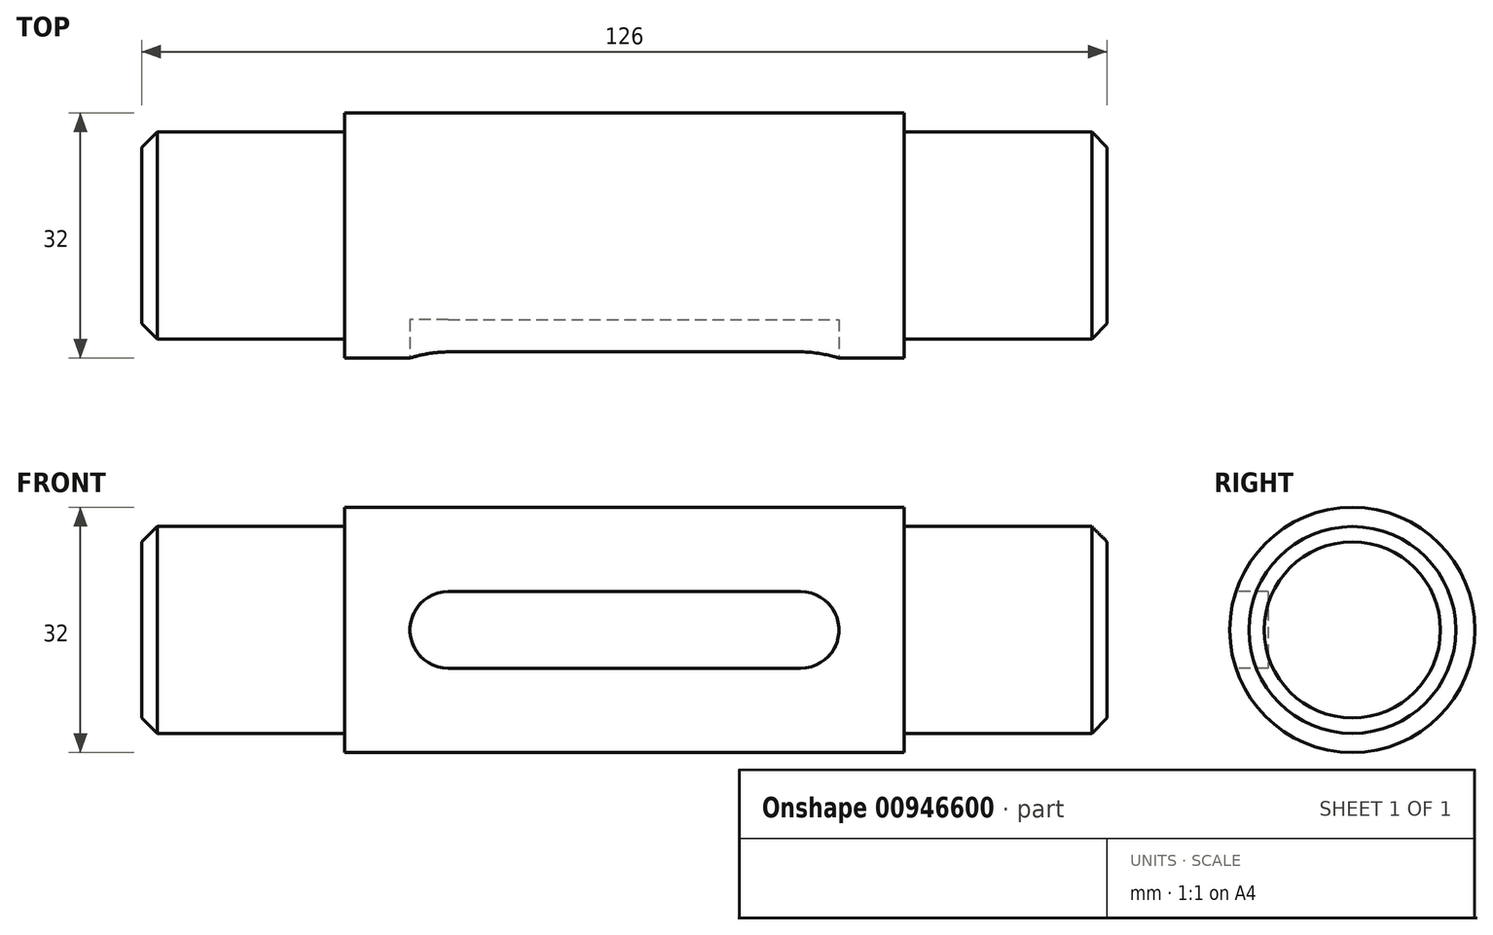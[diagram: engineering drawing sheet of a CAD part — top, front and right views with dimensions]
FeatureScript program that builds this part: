
annotation { "Feature Type Name" : "Feature", "Feature Type Description" : "" }
export const myFeature = defineFeature(function(context is Context, id is Id, definition is map)
    precondition{}
    {
        {
            var Q0;
            Q0=qCreatedBy(makeId("Front.planeOp"),FACE);
            var sketch = newSketch(context, id + "F0", { "sketchPlane" : qUnion([Q0])});
            skLineSegment(sketch, "E0", {"start": v(0, 16) * mm, "end": v(-36.5, 16) * mm});
            skLineSegment(sketch, "E1", {"start": v(-36.5, 16) * mm, "end": v(-36.5, 13.5) * mm});
            skLineSegment(sketch, "E2", {"start": v(-36.5, 13.5) * mm, "end": v(-61, 13.5) * mm});
            skLineSegment(sketch, "E3", {"start": v(-61, 13.5) * mm, "end": v(-63, 11.5) * mm});
            skLineSegment(sketch, "E4", {"start": v(-63, 11.5) * mm, "end": v(-63, 0) * mm});
            skLineSegment(sketch, "E5.MirrorCS", {"start": v(0, 16) * mm, "end": v(36.5, 16) * mm});
            skLineSegment(sketch, "E6.MirrorCS", {"start": v(36.5, 16) * mm, "end": v(36.5, 13.5) * mm});
            skLineSegment(sketch, "E7.MirrorCS", {"start": v(36.5, 13.5) * mm, "end": v(61, 13.5) * mm});
            skLineSegment(sketch, "E8.MirrorCS", {"start": v(61, 13.5) * mm, "end": v(63, 11.5) * mm});
            skLineSegment(sketch, "E9.MirrorCS", {"start": v(63, 11.5) * mm, "end": v(63, 0) * mm});
            skLineSegment(sketch, "E10", {"start": v(-63, 0) * mm, "end": v(63, 0) * mm});
            skSolve(sketch);
        }
        {
            var Q0;
            Q0 = qSketchRegion(id + "F0", true);
            var Q1;
            Q1=sQuery(id+"F0.wireOp",EDGE,"E10");
            revolve(context, id + "F1", {"surfaceOperationType" : NewSurfaceOperationType.NEW, "entities" : qUnion([Q0]), "axis" : qUnion([Q1]), "revolveType" : RevolveType.FULL});
        }
        {
            var Q0;
            Q0=qCreatedBy(makeId("Front.planeOp"),FACE);
            cPlane(context, id + "F2", {"entities" : qUnion([Q0]), "cplaneType" : CPlaneType.OFFSET, "offset" : 16 * mm, "width" : 150 * mm, "height" : 150 * mm});
        }
        {
            var Q0;
            Q0=qCreatedBy(id+"F2.planeOp",FACE);
            var sketch = newSketch(context, id + "F3", { "sketchPlane" : qUnion([Q0])});
            skLineSegment(sketch, "E11", {"start": v(-23, 0) * mm, "end": v(23, 0) * mm, "construction": true});
            skArc(sketch, "E12.0.startCap", {"start": v(-23, -5) * mm, "mid": v(-28, 0) * mm, "end": v(-23, 5) * mm});
            skArc(sketch, "E12.0.endCap", {"start": v(23, 5) * mm, "mid": v(28, 0) * mm, "end": v(23, -5) * mm});
            skLineSegment(sketch, "E12.0.left", {"start": v(-23, 5) * mm, "end": v(23, 5) * mm});
            skLineSegment(sketch, "E12.0.right", {"start": v(-23, -5) * mm, "end": v(23, -5) * mm});
            skSolve(sketch);
        }
        {
            var Q0;
            Q0 = qSketchRegion(id + "F3", true);
            extrude(context, id + "F4", {"entities" : qUnion([Q0]), "operationType" : NewBodyOperationType.REMOVE, "oppositeDirection" : true, "depth" : 5 * mm, "offsetDistance" : 25 * mm});
        }
    });
